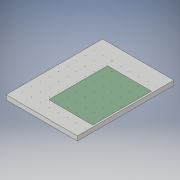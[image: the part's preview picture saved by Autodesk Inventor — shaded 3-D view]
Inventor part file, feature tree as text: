
AUTODESK INVENTOR PART (.ipt)
format: ipt  version: 2019.4 (Build 234330000, 330)  size: 216,576 bytes
history: native  units: in
note: dims shown in document units (in); Inventor stores cm internally (conversion verified against a paired STEP export)
features: sketch x3, extrude x2, hole x1
ambient origin geometry x8: Origin, YZ Plane, XZ Plane, XY Plane, X Axis, Y Axis, Z Axis, Center Point
bodies: Solid1 (feature_tree)
feature tree (6):
  extrude  "Extrusion1"  Depth=64.84in
  hole  "Hole1"  [1 undecoded]
  extrude  "Extrusion2"  Depth=0.001in
  sketch  "Sketch1"  dims[d0=48.0in d1=64.84in]
  sketch  "Sketch2"  dims[d2=3.0in d3=0.0in d4=0.25in]
  sketch  "Sketch3"  dims[d5=7.17in d6=2.0in d7=3.5433in d9=6.0in d10=3.1496in d12=6.0in d15=0.196in d16=0.5in d17=0.1575in d18=0.3937in d19=0.5635in d20=0.75in d21=0.8108in d22=31.17in d23=15.94in d24=39.3701in d25=29.5276in d26=0.001in d27=0.0in]
note: 1 required parameter value undecoded (feature->parameter linkage not recoverable at this tier; creation-order binding heuristic only, values carry confidence <= 0.55)
